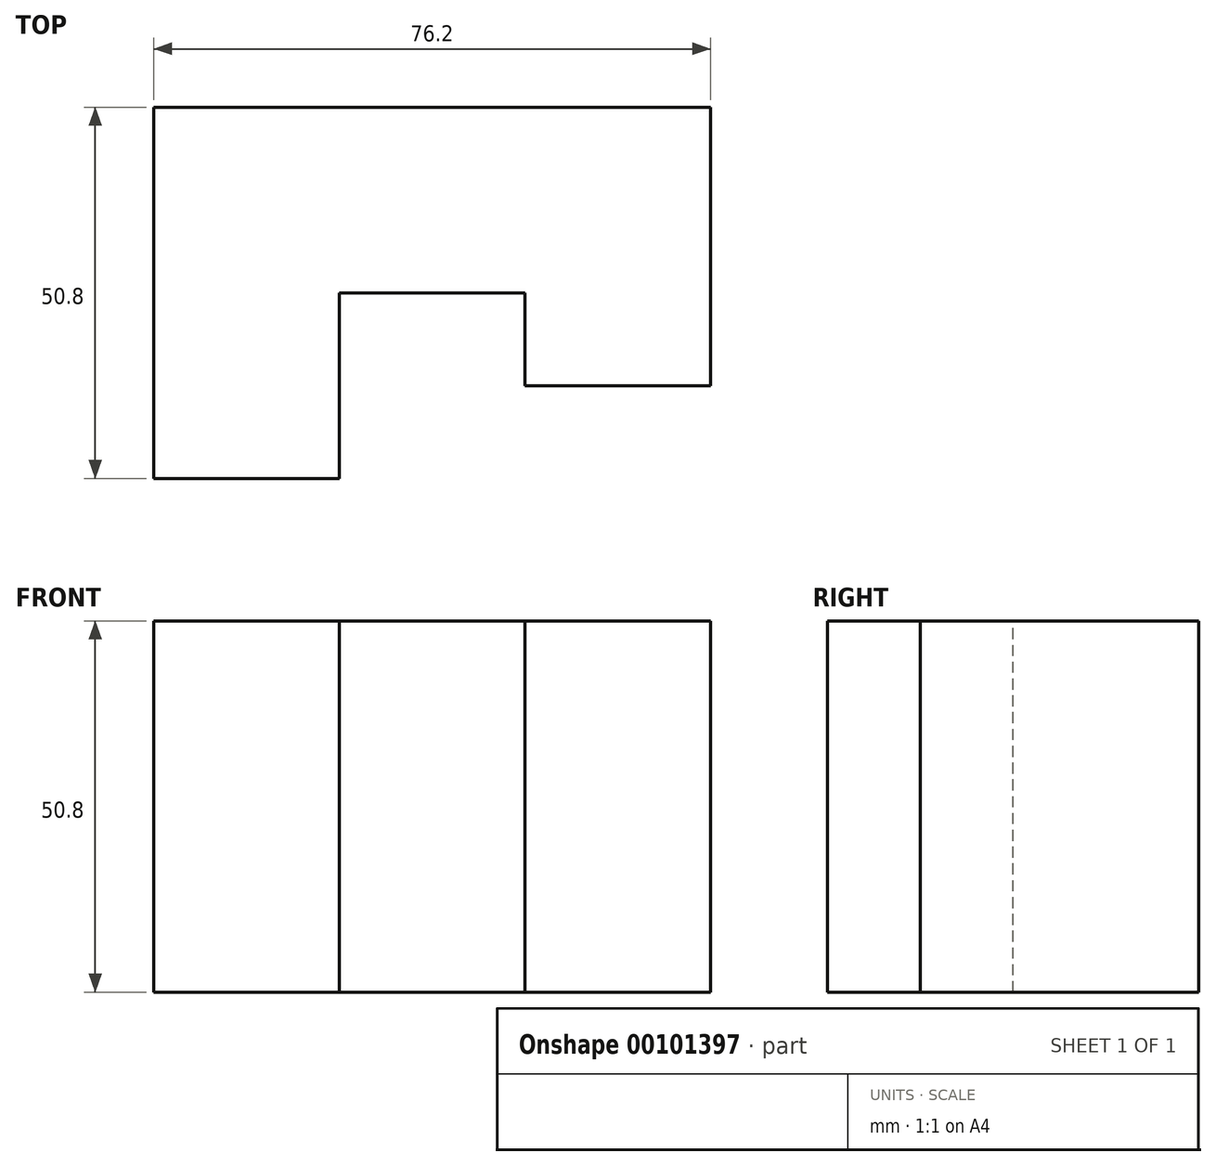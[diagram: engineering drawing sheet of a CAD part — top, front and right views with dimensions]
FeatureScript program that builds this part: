
annotation { "Feature Type Name" : "Feature", "Feature Type Description" : "" }
export const myFeature = defineFeature(function(context is Context, id is Id, definition is map)
    precondition{}
    {
        {
            var Q0;
            Q0=qCreatedBy(makeId("Front.planeOp"),FACE);
            var sketch = newSketch(context, id + "F0", { "sketchPlane" : qUnion([Q0])});
            skLineSegment(sketch, "E0", {"start": v(0, 0) * mm, "end": v(0, 50.8) * mm});
            skLineSegment(sketch, "E1", {"start": v(0, 50.8) * mm, "end": v(76.2, 50.8) * mm});
            skLineSegment(sketch, "E2", {"start": v(76.2, 50.8) * mm, "end": v(76.2, 0) * mm});
            skLineSegment(sketch, "E3", {"start": v(76.2, 0) * mm, "end": v(0, 0) * mm});
            skLineSegment(sketch, "E4", {"start": v(25.4, 50.8) * mm, "end": v(25.4, 0) * mm});
            skLineSegment(sketch, "E5", {"start": v(50.8, 0) * mm, "end": v(50.8, 20.51) * mm});
            skLineSegment(sketch, "E6", {"start": v(50.8, 20.51) * mm, "end": v(76.2, 20.51) * mm});
            skSolve(sketch);
        }
        {
            var Q0;
            Q0 = qSketchRegion(id + "F0", true);
            extrude(context, id + "F1", {"entities" : qUnion([Q0]), "oppositeDirection" : true, "depth" : 50.8 * mm});
        }
        {
            var Q0;
            Q0=makeQuery(id+"F1.opExtrude","SWEPT_FACE",FACE,{"disambiguationData":[OSD([sQuery(id+"F0.wireOp",EDGE,"E1")])]});
            var sketch = newSketch(context, id + "F2", { "sketchPlane" : qUnion([Q0])});
            skLineSegment(sketch, "E7", {"start": v(25.4, 0) * mm, "end": v(25.4, 25.4) * mm});
            skLineSegment(sketch, "E8", {"start": v(25.4, 25.4) * mm, "end": v(50.8, 25.4) * mm});
            skLineSegment(sketch, "E9", {"start": v(50.8, 25.4) * mm, "end": v(50.8, 12.7) * mm});
            skLineSegment(sketch, "E10", {"start": v(50.8, 12.7) * mm, "end": v(76.2, 12.7) * mm});
            skLineSegment(sketch, "E11", {"start": v(25.4, 0) * mm, "end": v(76.2, 0) * mm});
            skLineSegment(sketch, "E12", {"start": v(76.2, 0) * mm, "end": v(76.2, 12.7) * mm});
            skSolve(sketch);
        }
        {
            var Q0;
            Q0 = qSketchRegion(id + "F2", true);
            extrude(context, id + "F3", {"entities" : qUnion([Q0]), "operationType" : NewBodyOperationType.REMOVE, "oppositeDirection" : true, "depth" : 50.8 * mm});
        }
    });
